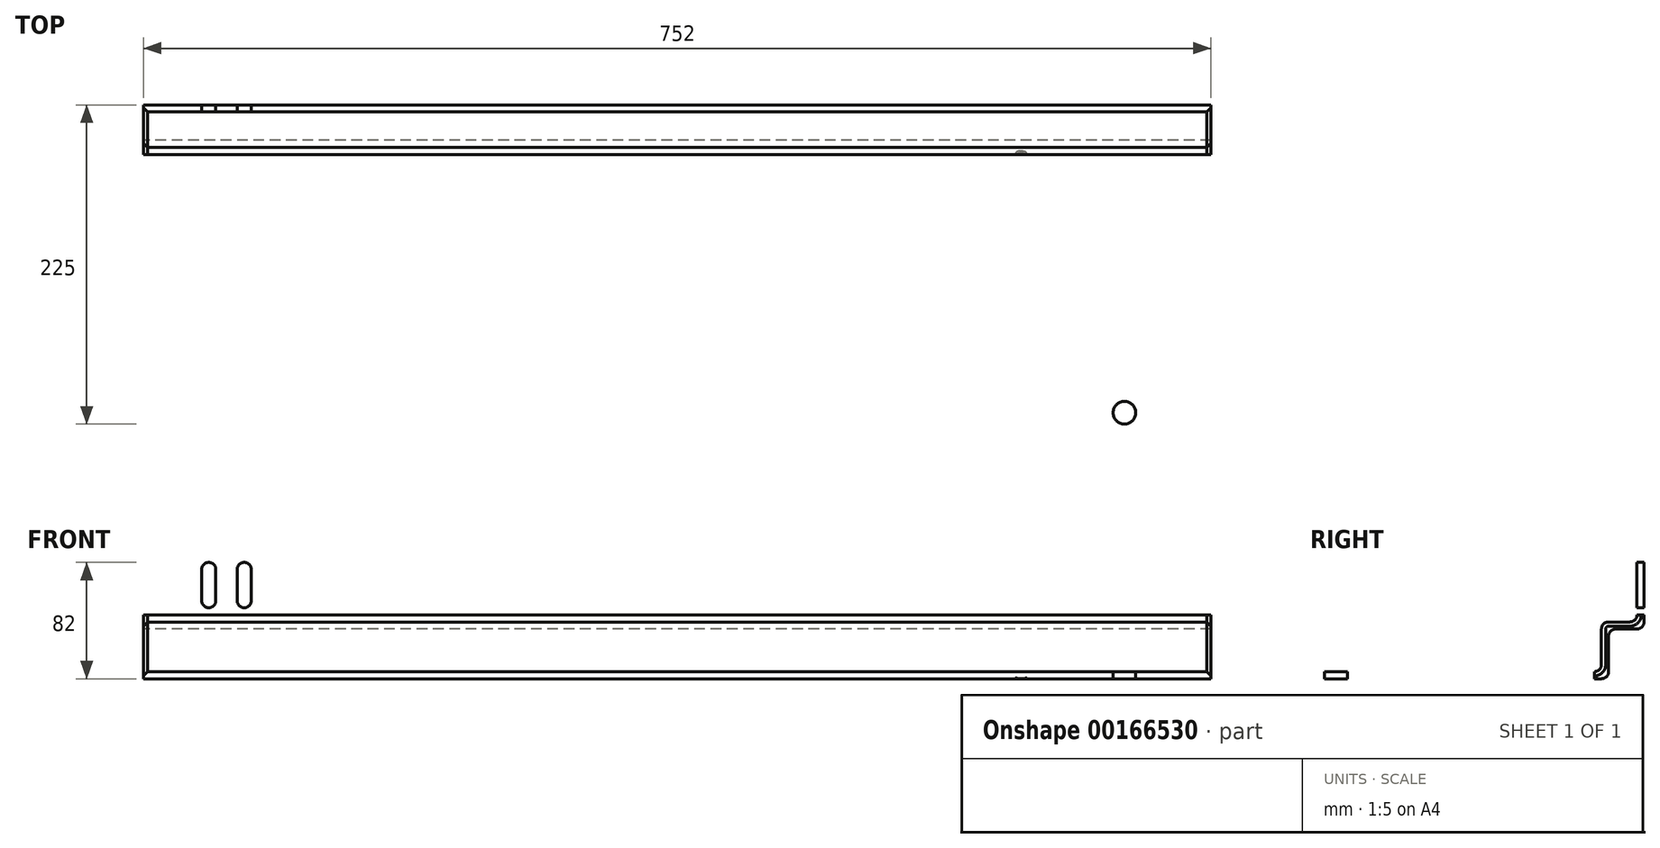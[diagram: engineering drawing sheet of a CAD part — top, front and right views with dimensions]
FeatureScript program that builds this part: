
annotation { "Feature Type Name" : "Feature", "Feature Type Description" : "" }
export const myFeature = defineFeature(function(context is Context, id is Id, definition is map)
    precondition{}
    {
        {
            var Q0;
            Q0=qCreatedBy(makeId("Right.planeOp"),FACE);
            var sketch = newSketch(context, id + "F0", { "sketchPlane" : qUnion([Q0])});
            skLineSegment(sketch, "E0", {"start": v(0, 0) * mm, "end": v(0, -60) * mm});
            skLineSegment(sketch, "E1", {"start": v(-5, -65) * mm, "end": v(-20, -65) * mm});
            skLineSegment(sketch, "E2", {"start": v(-25, -70) * mm, "end": v(-25, -95) * mm});
            skLineSegment(sketch, "E3", {"start": v(-30, -100) * mm, "end": v(-250, -100) * mm});
            skLineSegment(sketch, "E4", {"start": v(-250, -100) * mm, "end": v(-250, -95) * mm});
            skLineSegment(sketch, "E5", {"start": v(-250, -95) * mm, "end": v(-35, -95) * mm});
            skLineSegment(sketch, "E6", {"start": v(-30, -90) * mm, "end": v(-30, -65) * mm});
            skLineSegment(sketch, "E7", {"start": v(-25, -60) * mm, "end": v(-10, -60) * mm});
            skLineSegment(sketch, "E8", {"start": v(-5, -55) * mm, "end": v(-5, 0) * mm});
            skLineSegment(sketch, "E9", {"start": v(-5, 0) * mm, "end": v(0, 0) * mm});
            skPoint(sketch, "E10.visualSharp", {"position": v(-30, -95) * mm});
            skArc(sketch, "E10.filletArc", {"start": v(-35, -95) * mm, "mid": v(-31.46, -93.54) * mm, "end": v(-30, -90) * mm});
            skPoint(sketch, "E11.visualSharp", {"position": v(-25, -100) * mm});
            skArc(sketch, "E11.filletArc", {"start": v(-30, -100) * mm, "mid": v(-26.46, -98.54) * mm, "end": v(-25, -95) * mm});
            skPoint(sketch, "E12.visualSharp", {"position": v(-25, -65) * mm});
            skArc(sketch, "E12.filletArc", {"start": v(-20, -65) * mm, "mid": v(-23.54, -66.46) * mm, "end": v(-25, -70) * mm});
            skPoint(sketch, "E13.visualSharp", {"position": v(-30, -60) * mm});
            skArc(sketch, "E13.filletArc", {"start": v(-25, -60) * mm, "mid": v(-28.54, -61.46) * mm, "end": v(-30, -65) * mm});
            skPoint(sketch, "E14.visualSharp", {"position": v(-5, -60) * mm});
            skArc(sketch, "E14.filletArc", {"start": v(-10, -60) * mm, "mid": v(-6.46, -58.54) * mm, "end": v(-5, -55) * mm});
            skPoint(sketch, "E15.visualSharp", {"position": v(0, -65) * mm});
            skArc(sketch, "E15.filletArc", {"start": v(-5, -65) * mm, "mid": v(-1.46, -63.54) * mm, "end": v(0, -60) * mm});
            skPoint(sketch, "E16.visualSharp", {"position": v(-250, -95) * mm});
            skSolve(sketch);
        }
        {
            var Q0;
            Q0=makeQuery(id+"F0.imprint","IMPRINT",FACE,{"disambiguationData":[TD([[makeQuery(id+"F0.imprint","IMPRINT",EDGE,{"derivedFrom":sQuery(id+"F0.wireOp",EDGE,"E0")}),-1.0]])]});
            extrude(context, id + "F1", {"entities" : qUnion([Q0]), "depth" : 752 * mm});
        }
        {
            var Q0;
            Q0=makeQuery(id+"F1.opExtrude","SWEPT_FACE",FACE,{"disambiguationData":[OSD([sQuery(id+"F0.wireOp",EDGE,"E8")])]});
            var sketch = newSketch(context, id + "F2", { "sketchPlane" : qUnion([Q0])});
            skLineSegment(sketch, "E17", {"start": v(711, -23) * mm, "end": v(711, -45) * mm});
            skLineSegment(sketch, "E18", {"start": v(706, -50) * mm, "end": v(706, -50) * mm});
            skLineSegment(sketch, "E19", {"start": v(701, -45) * mm, "end": v(701, -23) * mm});
            skLineSegment(sketch, "E20", {"start": v(706, -18) * mm, "end": v(706, -18) * mm});
            skLineSegment(sketch, "E21", {"start": v(686, -23) * mm, "end": v(686, -45) * mm});
            skLineSegment(sketch, "E22", {"start": v(681, -50) * mm, "end": v(681, -50) * mm});
            skLineSegment(sketch, "E23", {"start": v(676, -45) * mm, "end": v(676, -23) * mm});
            skLineSegment(sketch, "E24", {"start": v(681, -18) * mm, "end": v(681, -18) * mm});
            skPoint(sketch, "E25.visualSharp", {"position": v(676, -18) * mm});
            skArc(sketch, "E25.filletArc", {"start": v(681, -18) * mm, "mid": v(677.46, -19.46) * mm, "end": v(676, -23) * mm});
            skPoint(sketch, "E26.visualSharp", {"position": v(676, -50) * mm});
            skArc(sketch, "E26.filletArc", {"start": v(676, -45) * mm, "mid": v(677.46, -48.54) * mm, "end": v(681, -50) * mm});
            skPoint(sketch, "E27.visualSharp", {"position": v(686, -50) * mm});
            skArc(sketch, "E27.filletArc", {"start": v(681, -50) * mm, "mid": v(684.54, -48.54) * mm, "end": v(686, -45) * mm});
            skPoint(sketch, "E28.visualSharp", {"position": v(686, -18) * mm});
            skArc(sketch, "E28.filletArc", {"start": v(686, -23) * mm, "mid": v(684.54, -19.46) * mm, "end": v(681, -18) * mm});
            skPoint(sketch, "E29.visualSharp", {"position": v(701, -18) * mm});
            skArc(sketch, "E29.filletArc", {"start": v(706, -18) * mm, "mid": v(702.46, -19.46) * mm, "end": v(701, -23) * mm});
            skPoint(sketch, "E30.visualSharp", {"position": v(711, -18) * mm});
            skArc(sketch, "E30.filletArc", {"start": v(711, -23) * mm, "mid": v(709.54, -19.46) * mm, "end": v(706, -18) * mm});
            skPoint(sketch, "E31.visualSharp", {"position": v(711, -50) * mm});
            skArc(sketch, "E31.filletArc", {"start": v(706, -50) * mm, "mid": v(709.54, -48.54) * mm, "end": v(711, -45) * mm});
            skPoint(sketch, "E32.visualSharp", {"position": v(701, -50) * mm});
            skArc(sketch, "E32.filletArc", {"start": v(701, -45) * mm, "mid": v(702.46, -48.54) * mm, "end": v(706, -50) * mm});
            skLineSegment(sketch, "E33", {"start": v(376, 0) * mm, "end": v(376, -55) * mm, "construction": true});
            skArc(sketch, "E34.MirrorCS", {"start": v(51, -45) * mm, "mid": v(49.54, -48.54) * mm, "end": v(46, -50) * mm});
            skArc(sketch, "E35.MirrorCS", {"start": v(71, -50) * mm, "mid": v(67.46, -48.54) * mm, "end": v(66, -45) * mm});
            skArc(sketch, "E36.MirrorCS", {"start": v(66, -23) * mm, "mid": v(67.46, -19.46) * mm, "end": v(71, -18) * mm});
            skArc(sketch, "E37.MirrorCS", {"start": v(46, -50) * mm, "mid": v(42.46, -48.54) * mm, "end": v(41, -45) * mm});
            skArc(sketch, "E38.MirrorCS", {"start": v(76, -45) * mm, "mid": v(74.54, -48.54) * mm, "end": v(71, -50) * mm});
            skArc(sketch, "E39.MirrorCS", {"start": v(41, -23) * mm, "mid": v(42.46, -19.46) * mm, "end": v(46, -18) * mm});
            skArc(sketch, "E40.MirrorCS", {"start": v(71, -18) * mm, "mid": v(74.54, -19.46) * mm, "end": v(76, -23) * mm});
            skLineSegment(sketch, "E41.MirrorCS", {"start": v(41, -23) * mm, "end": v(41, -45) * mm});
            skPoint(sketch, "E42.MirrorP", {"position": v(76, -50) * mm});
            skPoint(sketch, "E43.MirrorP", {"position": v(66, -18) * mm});
            skLineSegment(sketch, "E44.MirrorCS", {"start": v(66, -23) * mm, "end": v(66, -45) * mm});
            skPoint(sketch, "E45.MirrorP", {"position": v(41, -18) * mm});
            skPoint(sketch, "E46.MirrorP", {"position": v(51, -50) * mm});
            skLineSegment(sketch, "E47.MirrorCS", {"start": v(76, -45) * mm, "end": v(76, -23) * mm});
            skLineSegment(sketch, "E48.MirrorCS", {"start": v(51, -45) * mm, "end": v(51, -23) * mm});
            skPoint(sketch, "E49.MirrorP", {"position": v(76, -18) * mm});
            skPoint(sketch, "E50.MirrorP", {"position": v(41, -50) * mm});
            skPoint(sketch, "E51.MirrorP", {"position": v(66, -50) * mm});
            skPoint(sketch, "E52.MirrorP", {"position": v(51, -18) * mm});
            skArc(sketch, "E53.MirrorCS", {"start": v(46, -18) * mm, "mid": v(49.54, -19.46) * mm, "end": v(51, -23) * mm});
            skSolve(sketch);
        }
        {
            var Q0;
            Q0=makeQuery(id+"F2.imprint","IMPRINT",FACE,{"disambiguationData":[TD([[makeQuery(id+"F2.imprint","IMPRINT",EDGE,{"derivedFrom":sQuery(id+"F2.wireOp",EDGE,"E21")}),-1.0]])]});
            var Q1;
            Q1=makeQuery(id+"F2.imprint","IMPRINT",FACE,{"disambiguationData":[TD([[makeQuery(id+"F2.imprint","IMPRINT",EDGE,{"derivedFrom":sQuery(id+"F2.wireOp",EDGE,"E17")}),-1.0]])]});
            var Q2;
            Q2=makeQuery(id+"F2.imprint","IMPRINT",FACE,{"disambiguationData":[TD([[makeQuery(id+"F2.imprint","IMPRINT",EDGE,{"derivedFrom":sQuery(id+"F2.wireOp",EDGE,"E34.MirrorCS")}),-1.0]])]});
            var Q3;
            Q3=makeQuery(id+"F2.imprint","IMPRINT",FACE,{"disambiguationData":[TD([[makeQuery(id+"F2.imprint","IMPRINT",EDGE,{"derivedFrom":sQuery(id+"F2.wireOp",EDGE,"E35.MirrorCS")}),-1.0]])]});
            extrude(context, id + "F3", {"entities" : qUnion([Q0, Q1, Q2, Q3]), "operationType" : NewBodyOperationType.REMOVE, "endBound" : BoundingType.THROUGH_ALL, "oppositeDirection" : true, "depth" : 25 * mm});
        }
        {
            var Q0;
            Q0=makeQuery(id+"F1.opExtrude","SWEPT_FACE",FACE,{"disambiguationData":[OSD([sQuery(id+"F0.wireOp",EDGE,"E5")])]});
            var sketch = newSketch(context, id + "F4", { "sketchPlane" : qUnion([Q0])});
            skLineSegment(sketch, "E54", {"start": v(0, -217) * mm, "end": v(61, -217) * mm, "construction": true});
            skLineSegment(sketch, "E55", {"start": v(61, -217) * mm, "end": v(61, -250) * mm, "construction": true});
            skCircle(sketch, "E56", {"center": v(61, -217) * mm, "radius": 8 * mm});
            skLineSegment(sketch, "E57", {"start": v(376, -250) * mm, "end": v(376, -35) * mm, "construction": true});
            skCircle(sketch, "E58.MirrorC", {"center": v(691, -217) * mm, "radius": 8 * mm});
            skSolve(sketch);
        }
        {
            var Q0;
            Q0=makeQuery(id+"F1.opExtrude","SWEPT_EDGE",EDGE,{"disambiguationData":[OSD([sQuery(id+"F0.wireOp",EDGE,"E4"),sQuery(id+"F0.wireOp",EDGE,"E5")])]});
            chamfer(context, id + "F5", {"entities" : qUnion([Q0]), "width" : 3 * mm, "tangentPropagation" : true});
        }
        {
            var Q0;
            Q0=makeQuery(id+"F1.opExtrude","CAP_EDGE",EDGE,{"disambiguationData":[OSD([sQuery(id+"F0.wireOp",EDGE,"E5")])],"isStart":true});
            chamfer(context, id + "F6", {"entities" : qUnion([Q0]), "width" : 3 * mm, "tangentPropagation" : true});
        }
        {
            var Q0;
            Q0=makeQuery(id+"F1.opExtrude","CAP_EDGE",EDGE,{"disambiguationData":[OSD([sQuery(id+"F0.wireOp",EDGE,"E5")])],"isStart":false});
            chamfer(context, id + "F7", {"entities" : qUnion([Q0]), "width" : 3 * mm, "tangentPropagation" : true});
        }
        {
            var Q0;
            Q0=makeQuery(id+"F4.imprint","IMPRINT",FACE,{"disambiguationData":[TD([[makeQuery(id+"F4.imprint","IMPRINT",EDGE,{"derivedFrom":sQuery(id+"F4.wireOp",EDGE,"E56")}),1.0]])]});
            var Q1;
            Q1=makeQuery(id+"F4.imprint","IMPRINT",FACE,{"disambiguationData":[TD([[makeQuery(id+"F4.imprint","IMPRINT",EDGE,{"derivedFrom":sQuery(id+"F4.wireOp",EDGE,"E58.MirrorC")}),-1.0]])]});
            extrude(context, id + "F8", {"entities" : qUnion([Q0, Q1]), "operationType" : NewBodyOperationType.REMOVE, "oppositeDirection" : true, "depth" : 25 * mm});
        }
        {
            var Q0;
            Q0=makeQuery(id+"F1.opExtrude","SWEPT_FACE",FACE,{"disambiguationData":[OSD([sQuery(id+"F0.wireOp",EDGE,"E3")])]});
            var sketch = newSketch(context, id + "F9", { "sketchPlane" : qUnion([Q0])});
            skText(sketch, "E59", { "text": "Regalboden 75 cm", "fontName": "OpenSans-Regular.ttf"});
            const initialGuessF9  = {"E59": [0.59401, 0.03656, 1, 0, 0.0121]};
            skSetInitialGuess(sketch, initialGuessF9);
            skSolve(sketch);
        }
        {
            var Q0;
            Q0 = qSketchRegion(id + "F9", true);
            extrude(context, id + "F10", {"entities" : qUnion([Q0]), "operationType" : NewBodyOperationType.REMOVE, "oppositeDirection" : true, "depth" : 0.5 * mm});
        }
    });
